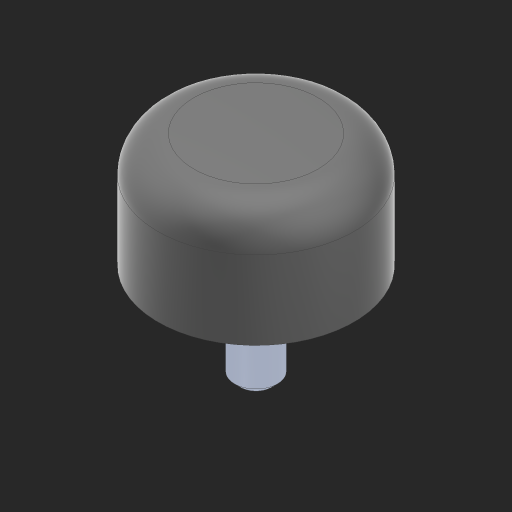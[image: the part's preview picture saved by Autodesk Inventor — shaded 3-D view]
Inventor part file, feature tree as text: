
AUTODESK INVENTOR PART (.ipt)
format: ipt  version: 2023 (Build 270158000, 158)  size: 183,808 bytes
history: native  units: in
note: dims shown in document units (in); Inventor stores cm internally (conversion verified against a paired STEP export)
features: sketch x2, helix x1, revolve x1, chamfer x1, boolean_combine x1
ambient origin geometry x8: Origin, YZ Plane, XZ Plane, XY Plane, X Axis, Y Axis, Z Axis, Center Point
bodies: Solid1 (feature_tree), Solid2 (feature_tree)
feature tree (6):
  helix  "Coil1"  [1 undecoded]
  revolve  "Revolution1"  Angle=30.0deg
  sketch  "Sketch1"  dims[d1=60.0deg d2=30.0deg]
  sketch  "Sketch2"  dims[d3=0.021in d4=0.031in d5=0.5in d6=0.3937in d7=0.0in d8=90.0deg d9=90.0deg d10=0.0in d11=0.0in d12=90.0deg]
  chamfer  "Chamfer1"  Angle=90.0deg  [1 undecoded]
  boolean_combine  "Combine2"
note: 2 required parameter values undecoded (feature->parameter linkage not recoverable at this tier; creation-order binding heuristic only, values carry confidence <= 0.55)
